# Revit family: Krowne_HS-22_WallMount_HandSink
name_source: partatom
category: Plumbing Fixtures
revit_build: Autodesk Revit 2018 (Build: 20190510_1515(x64)
units: mm (PartAtom-declared; Revit-internal decimal feet)

## family parameters
Always vertical = Yes
Cut with Voids When Loaded = No
OmniClass Number = 23.40.40.14.24.11
OmniClass Title = Bar Equipment
Part Type = Normal
Room Calculation Point = No
Round Connector Dimension = Use Diameter
Shared = No
Work Plane-Based = No

## types (1)
- HS-22
    Assembly Code = E1090320
    CSI MasterFormat = 11 46 13
    Cold Water Connection Height = 31 1/2"
    Cold Water Size = 1"
    Depth = 15"
    Description = 16"W Hand Sink with Royal Series Faucet
    Direct Waste Connection Height = 20"
    Direct Waste Size = 2"
    Foodservice Equipment Identifier = Yes
    Hot Water Connection Height = 31 1/2"
    Hot Water Size = 1"
    Hot Water Temperature = 110 °F
    Manufacturer = Krowne Metal
    Model = HS-22
    Sink Depth = 10"
    Sink Width = 10"
    URL = www.krowne.com
    Weight in Pounds = 16
    Width = 16"

## geometry (parser evidence)
native form markers: Sweep x3
no freeform markers — native parametric forms only
